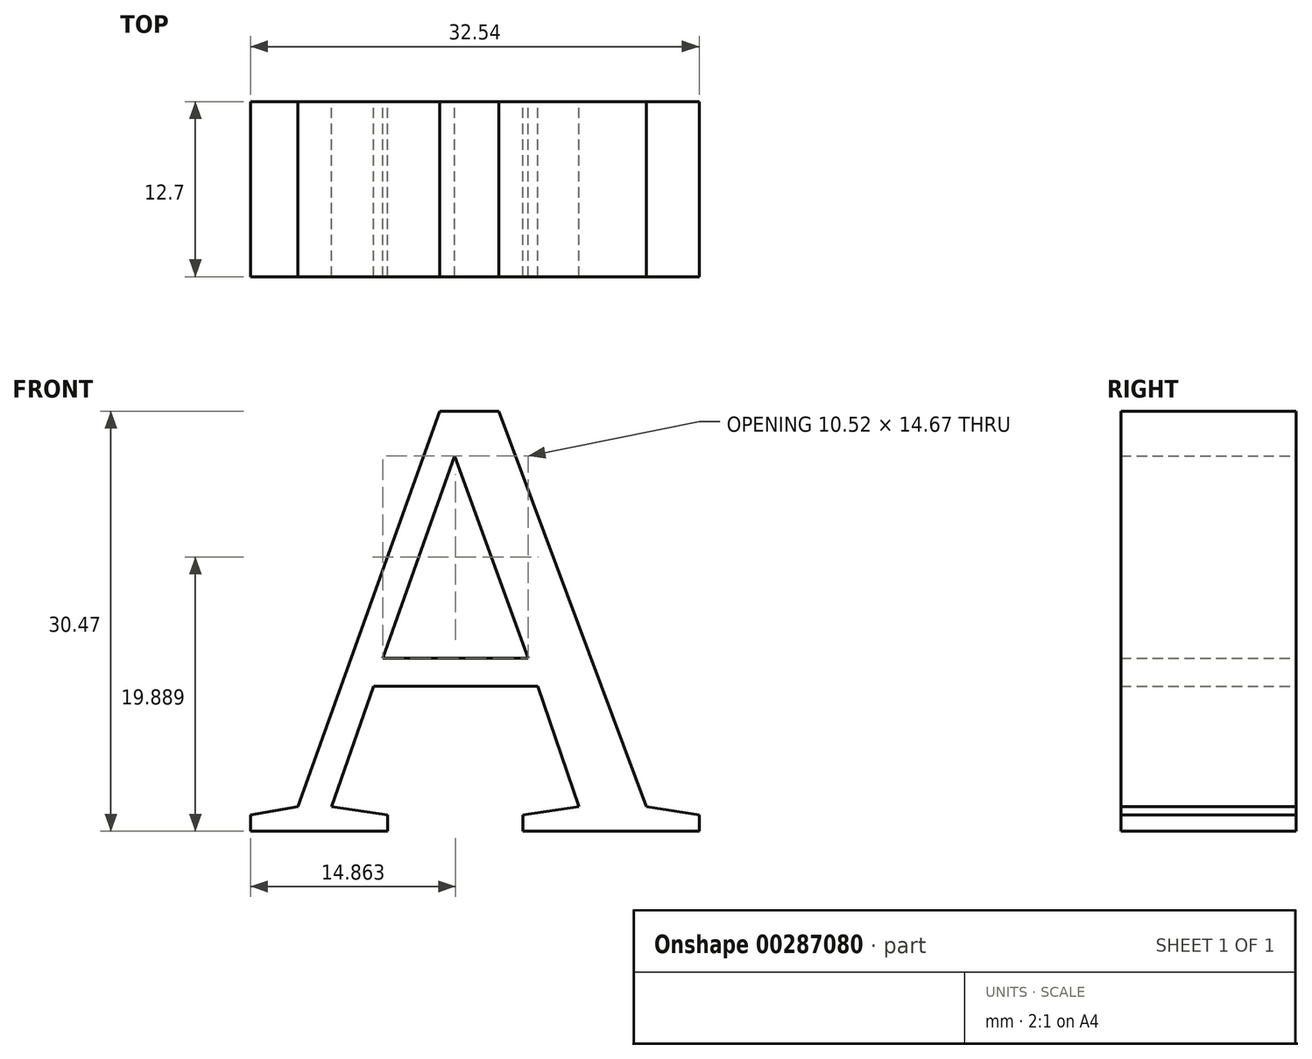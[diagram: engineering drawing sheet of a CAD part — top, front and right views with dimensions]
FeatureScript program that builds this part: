
annotation { "Feature Type Name" : "Feature", "Feature Type Description" : "" }
export const myFeature = defineFeature(function(context is Context, id is Id, definition is map)
    precondition{}
    {
        {
            var Q0;
            Q0=qCreatedBy(makeId("Front.planeOp"),FACE);
            var sketch = newSketch(context, id + "F0", { "sketchPlane" : qUnion([Q0])});
            skText(sketch, "E0", { "text": "A", "fontName": "Tinos-Regular.ttf"});
            const initialGuessF0  = {"E0": [-0.0464, 0.00325, 1, 0, 0.03323]};
            skSetInitialGuess(sketch, initialGuessF0);
            skSolve(sketch);
        }
        {
            var Q0;
            Q0 = qSketchRegion(id + "F0", true);
            extrude(context, id + "F1", {"entities" : qUnion([Q0]), "depth" : 12.7 * mm});
        }
    });
